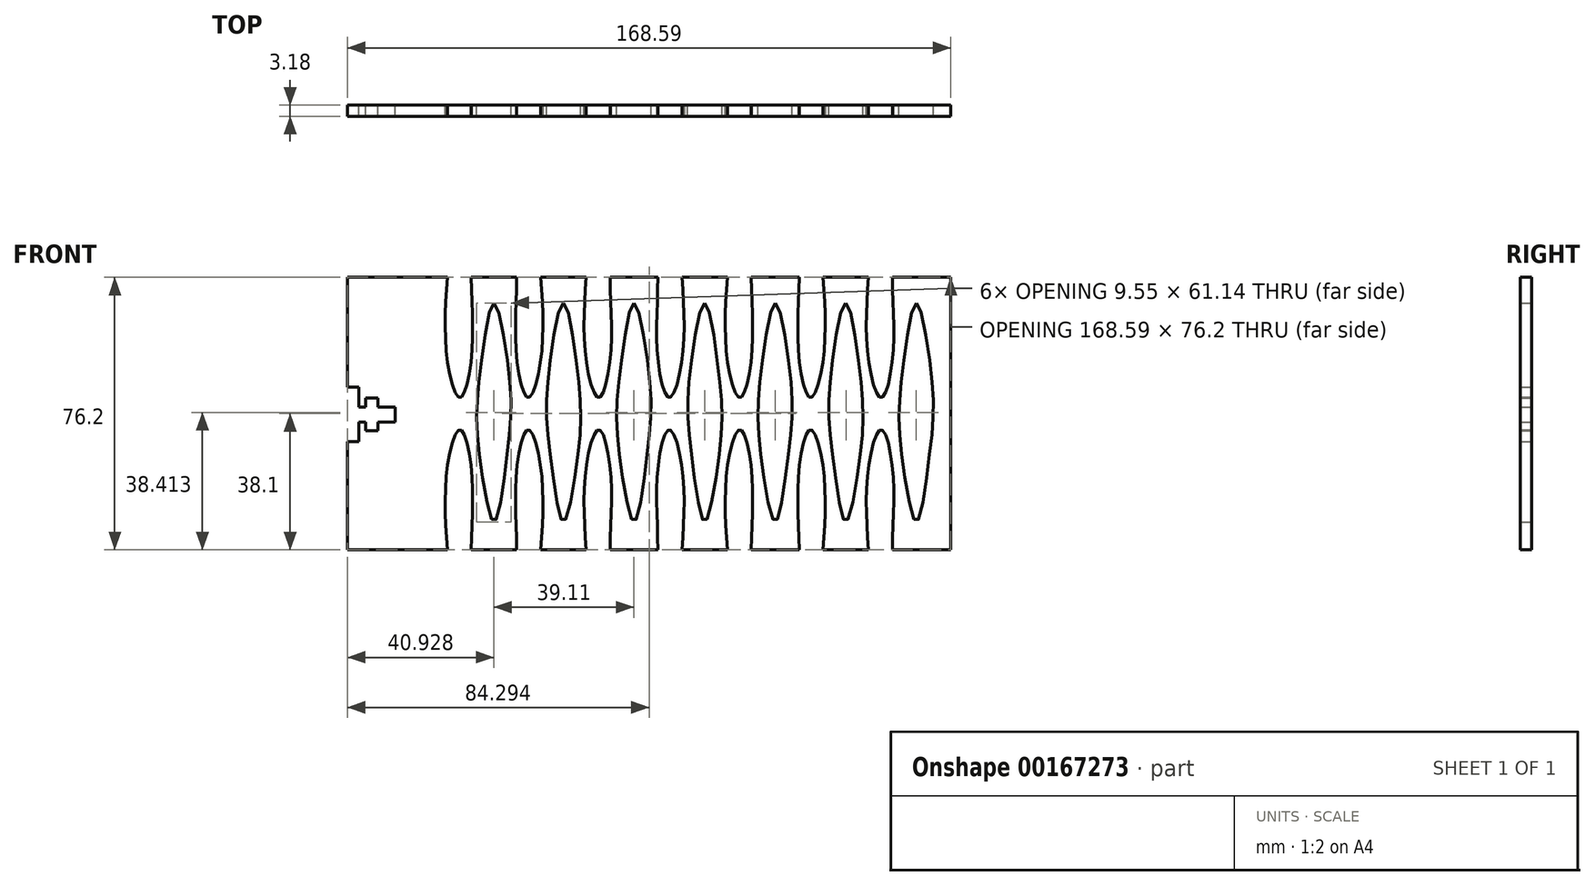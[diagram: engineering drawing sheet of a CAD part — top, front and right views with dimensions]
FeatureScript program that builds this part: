
annotation { "Feature Type Name" : "Feature", "Feature Type Description" : "" }
export const myFeature = defineFeature(function(context is Context, id is Id, definition is map)
    precondition{}
    {
        {
            var Q0;
            Q0=qCreatedBy(makeId("Front.planeOp"),FACE);
            var sketch = newSketch(context, id + "F0", { "sketchPlane" : qUnion([Q0])});
            skLineSegment(sketch, "E0", {"start": v(-56.83, 7.37) * mm, "end": v(-56.83, 38.1) * mm});
            skLineSegment(sketch, "E1", {"start": v(-56.83, -7.87) * mm, "end": v(-56.83, -38.1) * mm});
            skLineSegment(sketch, "E2.MirrorCS", {"start": v(-43.5, -2.33) * mm, "end": v(-48.27, -2.33) * mm});
            skLineSegment(sketch, "E3.MirrorCS", {"start": v(-43.5, 1.83) * mm, "end": v(-43.5, -2.33) * mm});
            skLineSegment(sketch, "E4.MirrorCS", {"start": v(-43.5, 1.83) * mm, "end": v(-48.27, 1.83) * mm});
            skLineSegment(sketch, "E5.MirrorCS", {"start": v(-48.27, 4.32) * mm, "end": v(-48.27, 1.83) * mm});
            skLineSegment(sketch, "E6.MirrorCS", {"start": v(-48.27, -2.33) * mm, "end": v(-48.27, -4.82) * mm});
            skLineSegment(sketch, "E7.MirrorCS", {"start": v(-51.75, -4.82) * mm, "end": v(-48.27, -4.82) * mm});
            skLineSegment(sketch, "E8.MirrorCS", {"start": v(-51.75, -2.33) * mm, "end": v(-51.75, -4.82) * mm});
            skLineSegment(sketch, "E9.MirrorCS", {"start": v(-51.75, 4.32) * mm, "end": v(-48.27, 4.32) * mm});
            skLineSegment(sketch, "E10.MirrorCS", {"start": v(-51.75, 4.32) * mm, "end": v(-51.75, 1.83) * mm});
            skLineSegment(sketch, "E11.MirrorCS", {"start": v(-51.75, -2.33) * mm, "end": v(-53.66, -2.33) * mm});
            skLineSegment(sketch, "E12.MirrorCS", {"start": v(-51.75, 1.83) * mm, "end": v(-53.66, 1.83) * mm});
            skLineSegment(sketch, "E13.MirrorCS", {"start": v(-53.66, 7.37) * mm, "end": v(-53.66, 1.83) * mm});
            skLineSegment(sketch, "E14.MirrorCS", {"start": v(-53.66, -2.33) * mm, "end": v(-53.66, -7.87) * mm});
            skLineSegment(sketch, "E15.MirrorCS", {"start": v(-53.66, 7.37) * mm, "end": v(-56.83, 7.37) * mm});
            skLineSegment(sketch, "E16.MirrorCS", {"start": v(-53.66, -7.87) * mm, "end": v(-56.83, -7.87) * mm});
            skLineSegment(sketch, "E17", {"start": v(-56.83, 38.1) * mm, "end": v(-28.9, 38.1) * mm});
            skLineSegment(sketch, "E18.MirrorCS", {"start": v(-56.83, -38.1) * mm, "end": v(-28.9, -38.1) * mm});
            skFitSpline(sketch, "E19", {"points": [v(-28.9, -38.1) * mm, v(-28.9, -14.86) * mm, v(-25.38, -4.48) * mm, v(-22.2, -15.27) * mm, v(-22.2, -38.1) * mm], "startDerivative": vector(-5.55, 78.76) * mm, "endDerivative": vector(-1.02, -78.66) * mm});
            skLineSegment(sketch, "E20", {"start": v(-22.2, -38.1) * mm, "end": v(-9.5, -38.1) * mm});
            skFitSpline(sketch, "E21.MirrorCS", {"points": [v(-28.9, 38.1) * mm, v(-28.9, 14.86) * mm, v(-25.38, 4.48) * mm, v(-22.2, 15.27) * mm, v(-22.2, 38.1) * mm], "startDerivative": vector(-5.55, -78.76) * mm, "endDerivative": vector(-1.02, 78.66) * mm});
            skLineSegment(sketch, "E22.MirrorCS", {"start": v(-22.2, 38.1) * mm, "end": v(-9.5, 38.1) * mm});
            skFitSpline(sketch, "E23", {"points": [v(-15.85, 30.88) * mm, v(-19.27, 15.7) * mm, v(-20.68, 0) * mm, v(-19.38, -15.48) * mm, v(-15.85, -30.26) * mm, v(-12.74, -15.73) * mm, v(-11.13, 0) * mm, v(-12.24, 15.59) * mm, v(-15.85, 30.88) * mm]});
            skFitSpline(sketch, "E24.MirrorCS", {"points": [v(-2.8, 38.1) * mm, v(-2.8, 14.86) * mm, v(-6.32, 4.48) * mm, v(-9.5, 15.27) * mm, v(-9.5, 38.1) * mm], "startDerivative": vector(5.55, -78.76) * mm, "endDerivative": vector(1.02, 78.66) * mm});
            skFitSpline(sketch, "E25.MirrorCS", {"points": [v(-2.8, -38.1) * mm, v(-2.8, -14.86) * mm, v(-6.32, -4.48) * mm, v(-9.5, -15.27) * mm, v(-9.5, -38.1) * mm], "startDerivative": vector(5.55, 78.76) * mm, "endDerivative": vector(1.02, -78.66) * mm});
            skFitSpline(sketch, "E26.MirrorC", {"points": [v(3.54, 30.88) * mm, v(6.96, 15.7) * mm, v(8.37, 0) * mm, v(7.07, -15.48) * mm, v(3.54, -30.26) * mm, v(0.43, -15.73) * mm, v(-1.18, 0) * mm, v(-0.07, 15.59) * mm, v(3.54, 30.88) * mm]});
            skFitSpline(sketch, "E27.MirrorCS", {"points": [v(9.9, 38.1) * mm, v(9.9, 14.86) * mm, v(13.4, 4.48) * mm, v(16.58, 15.27) * mm, v(16.58, 38.1) * mm], "startDerivative": vector(-5.55, -78.76) * mm, "endDerivative": vector(-1.02, 78.66) * mm});
            skFitSpline(sketch, "E28.MirrorCS", {"points": [v(9.9, -38.1) * mm, v(9.9, -14.86) * mm, v(13.4, -4.48) * mm, v(16.58, -15.27) * mm, v(16.58, -38.1) * mm], "startDerivative": vector(-5.55, 78.76) * mm, "endDerivative": vector(-1.02, -78.66) * mm});
            skFitSpline(sketch, "E29.MirrorC", {"points": [v(23.26, 30.88) * mm, v(19.84, 15.7) * mm, v(18.43, 0) * mm, v(19.73, -15.48) * mm, v(23.26, -30.26) * mm, v(26.38, -15.73) * mm, v(27.98, 0) * mm, v(26.87, 15.59) * mm, v(23.26, 30.88) * mm]});
            skFitSpline(sketch, "E30.MirrorCS", {"points": [v(36.63, 38.1) * mm, v(36.63, 14.86) * mm, v(33.12, 4.48) * mm, v(29.94, 15.27) * mm, v(29.94, 38.1) * mm], "startDerivative": vector(5.55, -78.76) * mm, "endDerivative": vector(1.02, 78.66) * mm});
            skFitSpline(sketch, "E31.MirrorCS", {"points": [v(36.63, -38.1) * mm, v(36.63, -14.86) * mm, v(33.12, -4.48) * mm, v(29.94, -15.27) * mm, v(29.94, -38.1) * mm], "startDerivative": vector(5.55, 78.76) * mm, "endDerivative": vector(1.02, -78.66) * mm});
            skFitSpline(sketch, "E32.MirrorC", {"points": [v(42.98, 30.88) * mm, v(46.4, 15.7) * mm, v(47.8, 0) * mm, v(46.51, -15.48) * mm, v(42.98, -30.26) * mm, v(39.86, -15.73) * mm, v(38.26, 0) * mm, v(39.37, 15.59) * mm, v(42.98, 30.88) * mm]});
            skFitSpline(sketch, "E33.MirrorCS", {"points": [v(49.33, 38.1) * mm, v(49.33, 14.86) * mm, v(52.84, 4.48) * mm, v(56.02, 15.27) * mm, v(56.02, 38.1) * mm], "startDerivative": vector(-5.55, -78.76) * mm, "endDerivative": vector(-1.02, 78.66) * mm});
            skFitSpline(sketch, "E34.MirrorCS", {"points": [v(49.33, -38.1) * mm, v(49.33, -14.86) * mm, v(52.84, -4.48) * mm, v(56.02, -15.27) * mm, v(56.02, -38.1) * mm], "startDerivative": vector(-5.55, 78.76) * mm, "endDerivative": vector(-1.02, -78.66) * mm});
            skFitSpline(sketch, "E35.MirrorC", {"points": [v(62.7, 30.88) * mm, v(59.28, 15.7) * mm, v(57.87, 0) * mm, v(59.16, -15.48) * mm, v(62.7, -30.26) * mm, v(65.81, -15.73) * mm, v(67.41, 0) * mm, v(66.3, 15.59) * mm, v(62.7, 30.88) * mm]});
            skFitSpline(sketch, "E36.MirrorCS", {"points": [v(76.07, 38.1) * mm, v(76.07, 14.86) * mm, v(72.56, 4.48) * mm, v(69.37, 15.27) * mm, v(69.37, 38.1) * mm], "startDerivative": vector(5.55, -78.76) * mm, "endDerivative": vector(1.02, 78.66) * mm});
            skFitSpline(sketch, "E37.MirrorCS", {"points": [v(76.07, -38.1) * mm, v(76.07, -14.86) * mm, v(72.56, -4.48) * mm, v(69.37, -15.27) * mm, v(69.37, -38.1) * mm], "startDerivative": vector(5.55, 78.76) * mm, "endDerivative": vector(1.02, -78.66) * mm});
            skFitSpline(sketch, "E38.MirrorC", {"points": [v(82.42, 30.88) * mm, v(85.83, 15.7) * mm, v(87.24, 0) * mm, v(85.95, -15.48) * mm, v(82.42, -30.26) * mm, v(79.3, -15.73) * mm, v(77.7, 0) * mm, v(78.8, 15.59) * mm, v(82.42, 30.88) * mm]});
            skFitSpline(sketch, "E39.MirrorCS", {"points": [v(88.77, 38.1) * mm, v(88.77, 14.86) * mm, v(92.27, 4.48) * mm, v(95.46, 15.27) * mm, v(95.46, 38.1) * mm], "startDerivative": vector(-5.55, -78.76) * mm, "endDerivative": vector(-1.02, 78.66) * mm});
            skFitSpline(sketch, "E40.MirrorCS", {"points": [v(88.77, -38.1) * mm, v(88.77, -14.86) * mm, v(92.27, -4.48) * mm, v(95.46, -15.27) * mm, v(95.46, -38.1) * mm], "startDerivative": vector(-5.55, 78.76) * mm, "endDerivative": vector(-1.02, -78.66) * mm});
            skFitSpline(sketch, "E41.MirrorC", {"points": [v(102.13, 30.88) * mm, v(98.72, 15.7) * mm, v(97.3, 0) * mm, v(98.6, -15.48) * mm, v(102.13, -30.26) * mm, v(105.25, -15.73) * mm, v(106.85, 0) * mm, v(105.74, 15.59) * mm, v(102.13, 30.88) * mm]});
            skLineSegment(sketch, "E42", {"start": v(95.46, 38.1) * mm, "end": v(111.76, 38.1) * mm});
            skLineSegment(sketch, "E43", {"start": v(111.76, 38.1) * mm, "end": v(111.76, -38.1) * mm});
            skLineSegment(sketch, "E44", {"start": v(111.76, -38.1) * mm, "end": v(95.46, -38.1) * mm});
            skLineSegment(sketch, "E45", {"start": v(88.77, -38.1) * mm, "end": v(76.07, -38.1) * mm});
            skLineSegment(sketch, "E46", {"start": v(69.37, -38.1) * mm, "end": v(56.02, -38.1) * mm});
            skLineSegment(sketch, "E47", {"start": v(49.33, -38.1) * mm, "end": v(36.63, -38.1) * mm});
            skLineSegment(sketch, "E48", {"start": v(29.94, -38.1) * mm, "end": v(16.58, -38.1) * mm});
            skLineSegment(sketch, "E49", {"start": v(9.9, -38.1) * mm, "end": v(-2.8, -38.1) * mm});
            skLineSegment(sketch, "E50", {"start": v(-2.8, 38.1) * mm, "end": v(9.9, 38.1) * mm});
            skLineSegment(sketch, "E51", {"start": v(16.58, 38.1) * mm, "end": v(29.94, 38.1) * mm});
            skLineSegment(sketch, "E52", {"start": v(36.63, 38.1) * mm, "end": v(49.33, 38.1) * mm});
            skLineSegment(sketch, "E53", {"start": v(56.02, 38.1) * mm, "end": v(69.37, 38.1) * mm});
            skLineSegment(sketch, "E54", {"start": v(76.07, 38.1) * mm, "end": v(88.77, 38.1) * mm});
            skSolve(sketch);
        }
        {
            var Q0;
            Q0 = qSketchRegion(id + "F0", true);
            extrude(context, id + "F1", {"entities" : qUnion([Q0]), "depth" : 3.17 * mm});
        }
    });
